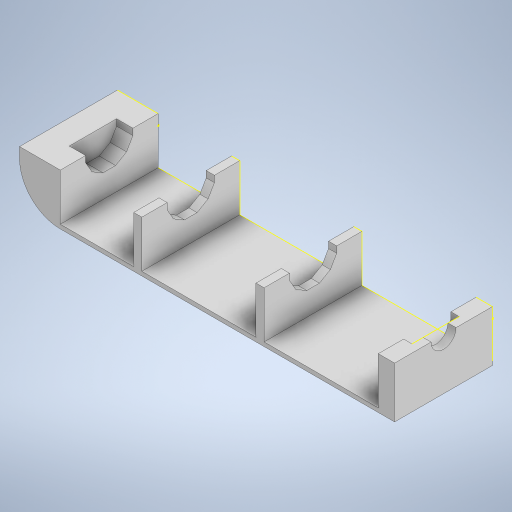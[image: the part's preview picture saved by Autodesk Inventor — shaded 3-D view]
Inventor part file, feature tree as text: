
AUTODESK INVENTOR PART (.ipt)
format: ipt  version: 2023 (Build 270158000, 158)  size: 339,968 bytes
history: native  units: in
note: dims shown in document units (in); Inventor stores cm internally (conversion verified against a paired STEP export)
features: sketch x9, extrude x5, projected_geometry x2, other x1
ambient origin geometry x8: Origin, YZ Plane, XZ Plane, XY Plane, X Axis, Y Axis, Z Axis, Center Point
bodies: Body1 (feature_tree)
feature tree (17):
  other  "솔리드1"
  sketch  "스케치1"
  sketch  "스케치2"
  sketch  "스케치3"
  extrude  "돌출1"  Depth=0.7874in
  extrude  "돌출2"  Depth=0.0984in
  sketch  "스케치4"
  extrude  "돌출3"  Depth=0.4528in
  extrude  "돌출4"  Depth=0.7087in
  sketch  "스케치7"
  sketch  "스케치8"
  extrude  "돌출5"  Depth=0.0787in
  sketch  "스케치5"
  sketch  "스케치6"
  projected_geometry  "투영된 루프1"
  projected_geometry  "투영된 루프2"
  sketch  "스케치9"
